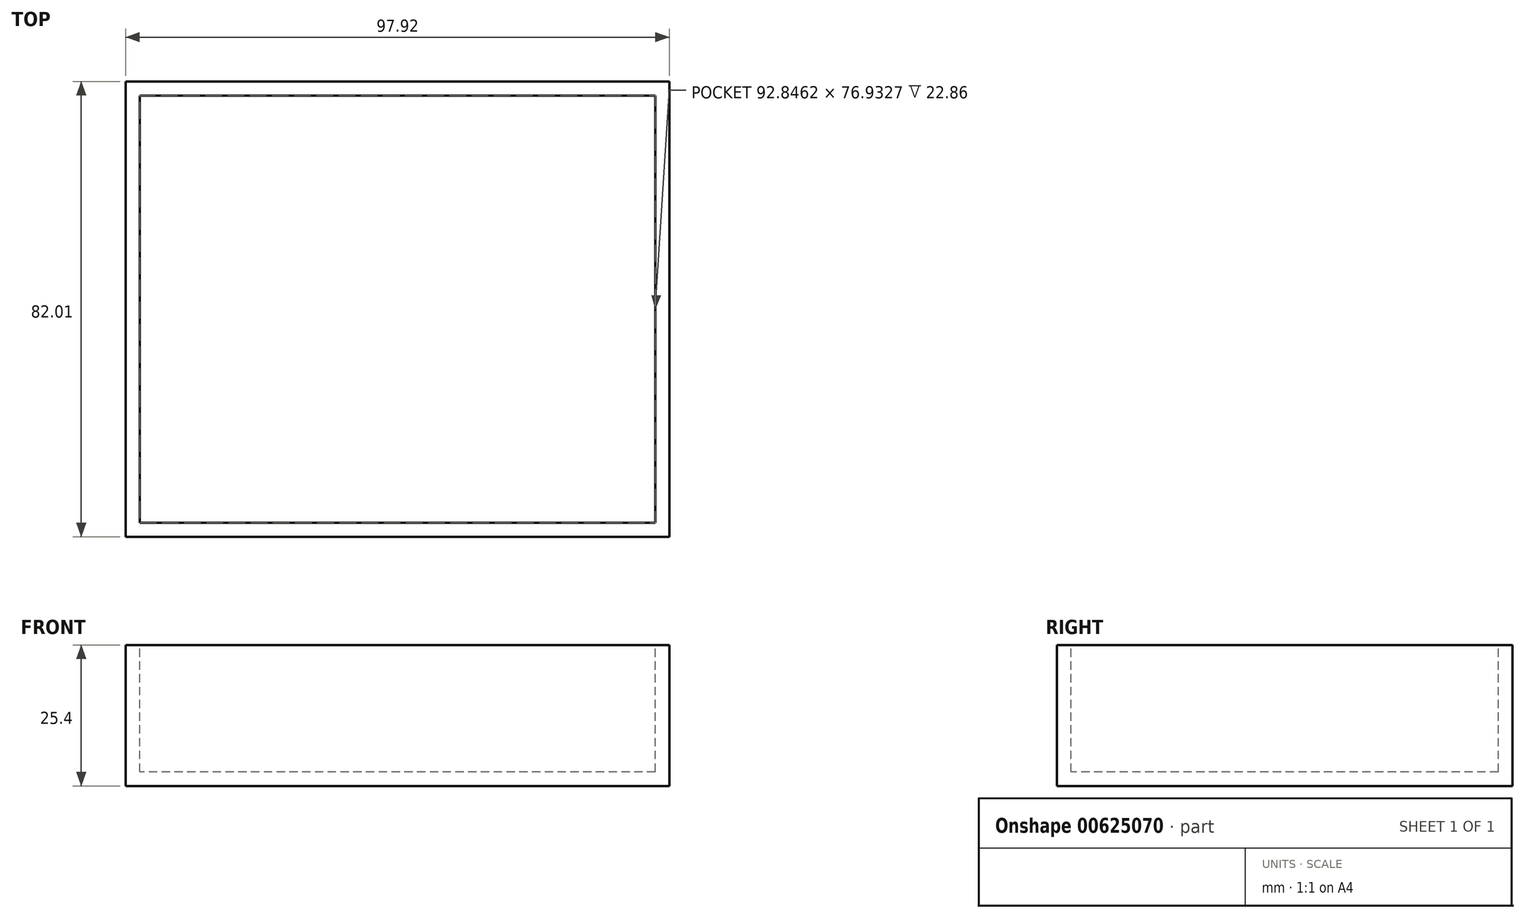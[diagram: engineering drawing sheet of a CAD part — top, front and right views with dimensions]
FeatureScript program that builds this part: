
annotation { "Feature Type Name" : "Feature", "Feature Type Description" : "" }
export const myFeature = defineFeature(function(context is Context, id is Id, definition is map)
    precondition{}
    {
        {
            var Q0;
            Q0=qCreatedBy(makeId("Top.planeOp"),FACE);
            var sketch = newSketch(context, id + "F0", { "sketchPlane" : qUnion([Q0])});
            skLineSegment(sketch, "E0.bottom", {"start": v(48.96, 68.31) * mm, "end": v(-48.96, 68.31) * mm});
            skLineSegment(sketch, "E0.top", {"start": v(48.96, -68.31) * mm, "end": v(-48.96, -68.31) * mm});
            skLineSegment(sketch, "E0.left", {"start": v(48.96, 68.31) * mm, "end": v(48.96, -68.31) * mm});
            skLineSegment(sketch, "E0.right", {"start": v(-48.96, 68.31) * mm, "end": v(-48.96, -68.31) * mm});
            skPoint(sketch, "E0.middle", {"position": v(0, 0) * mm});
            skSolve(sketch);
        }
        {
            var Q0;
            Q0=sQuery(id+"F0.wireOp",EDGE,"E0.top");
            extrude(context, id + "F1", {"bodyType" : ToolBodyType.SURFACE, "surfaceEntities" : qUnion([Q0]), "depth" : 25.4 * mm, "offsetDistance" : 25.4 * mm});
        }
        {
            var Q0;
            Q0=makeQuery(id+"F1.opExtrude","SWEPT_FACE",FACE,{"disambiguationData":[OSD([sQuery(id+"F0.wireOp",EDGE,"E0.top")])]});
            var sketch = newSketch(context, id + "F2", { "sketchPlane" : qUnion([Q0])});
            skSolve(sketch);
        }
        {
            var Q0;
            Q0 = qSketchRegion(id + "F2", true);
            var Q1;
            Q1=makeQuery(id+"F2.imprint","IMPRINT",FACE,{"disambiguationData":[TD([[makeQuery(id+"F2.imprint","IMPRINT",EDGE,{"derivedFrom":makeQuery(id+"F1.opExtrude","SWEPT_EDGE",EDGE,{"disambiguationData":[OSD([sQuery(id+"F0.wireOp",VERTEX,"E0.top.start")])]})}),-1.0]])]});
            extrude(context, id + "F3", {"entities" : qUnion([Q0, Q1]), "depth" : 82.01 * mm, "offsetDistance" : 25.4 * mm});
        }
        {
            var Q0;
            {var subQ0=sQuery(id+"F0.wireOp",EDGE,"E0.top");Q0=makeQuery(id+"F3.opExtrude","SWEPT_FACE",FACE,{"disambiguationData":[OSD([subQ0]),TDD([makeQuery(id+"F2.imprint","IMPRINT",EDGE,{"derivedFrom":makeQuery(id+"F1.opExtrude","CAP_EDGE",EDGE,{"disambiguationData":[OSD([subQ0])],"isStart":false})})])]});}
            shell(context, id + "F4", {"entities" : qUnion([Q0]), "thickness" : 2.54 * mm});
        }
        {
            var Q0;
            Q0=makeQuery(id+"F4.opShell","OFFSET_FACE",FACE,{"disambiguationData":[OSD([sQuery(id+"F0.wireOp",EDGE,"E0.top")])]});
            var sketch = newSketch(context, id + "F5", { "sketchPlane" : qUnion([Q0])});
            skLineSegment(sketch, "E1", {"start": v(-46.42, 11.16) * mm, "end": v(46.42, -65.77) * mm});
            skSolve(sketch);
        }
        {
            var Q0;
            Q0=sQuery(id+"F5.wireOp",EDGE,"E1");
            extrude(context, id + "F6", {"bodyType" : ToolBodyType.SURFACE, "surfaceEntities" : qUnion([Q0]), "depth" : 23.5 * mm, "offsetDistance" : 25.4 * mm});
        }
        {
            var Q0;
            Q0=makeQuery(id+"F4.opShell","OFFSET_FACE",FACE,{"disambiguationData":[OSD([sQuery(id+"F0.wireOp",EDGE,"E0.top")])]});
            var sketch = newSketch(context, id + "F7", { "sketchPlane" : qUnion([Q0])});
            skLineSegment(sketch, "E2", {"start": v(-46.42, -65.77) * mm, "end": v(46.42, 11.16) * mm});
            skSolve(sketch);
        }
        {
            var Q0;
            Q0=makeQuery(id+"F5.imprint","IMPRINT",FACE,{"disambiguationData":[TD([[makeQuery(id+"F5.imprint","IMPRINT",EDGE,{"derivedFrom":sQuery(id+"F5.wireOp",EDGE,"E1")}),-1.0]])]});
            var sketch = newSketch(context, id + "F8", { "sketchPlane" : qUnion([Q0])});
            skSolve(sketch);
        }
        {
            var Q0;
            Q0=makeQuery(id+"F8.imprint","IMPRINT",FACE,{"disambiguationData":[TD([[makeQuery(id+"F8.imprint","IMPRINT",EDGE,{"derivedFrom":makeQuery(id+"F5.imprint","IMPRINT",EDGE,{"derivedFrom":sQuery(id+"F5.wireOp",EDGE,"E1")})}),-1.0]])]});
            var sketch = newSketch(context, id + "F9", { "sketchPlane" : qUnion([Q0])});
            skLineSegment(sketch, "E3.bottom", {"start": v(-10.82, -30.24) * mm, "end": v(10.82, -30.24) * mm});
            skLineSegment(sketch, "E3.top", {"start": v(-10.82, -24.14) * mm, "end": v(10.82, -24.14) * mm});
            skLineSegment(sketch, "E3.left", {"start": v(-10.82, -30.24) * mm, "end": v(-10.82, -24.14) * mm});
            skLineSegment(sketch, "E3.right", {"start": v(10.82, -30.24) * mm, "end": v(10.82, -24.14) * mm});
            skPoint(sketch, "E3.middle", {"position": v(0, -27.2) * mm});
            skSolve(sketch);
        }
        {
            var Q0;
            Q0=sQuery(id+"F9.wireOp",EDGE,"E3.left");
            var Q1;
            Q1=sQuery(id+"F9.wireOp",EDGE,"E3.top");
            var Q2;
            Q2=sQuery(id+"F9.wireOp",EDGE,"E3.right");
            var Q3;
            Q3=sQuery(id+"F9.wireOp",EDGE,"E3.bottom");
            extrude(context, id + "F10", {"bodyType" : ToolBodyType.SURFACE, "surfaceEntities" : qUnion([Q0, Q1, Q2, Q3]), "depth" : 24.24 * mm, "offsetDistance" : 25.4 * mm});
        }
        {
            var Q0;
            Q0=makeQuery(id+"F6.opExtrude","SWEPT_BODY",BODY,{"disambiguationData":[OSD([sQuery(id+"F5.wireOp",EDGE,"E1")])]});
            deleteBodies(context, id + "F11", {"entities" : qUnion([Q0])});
        }
    });
